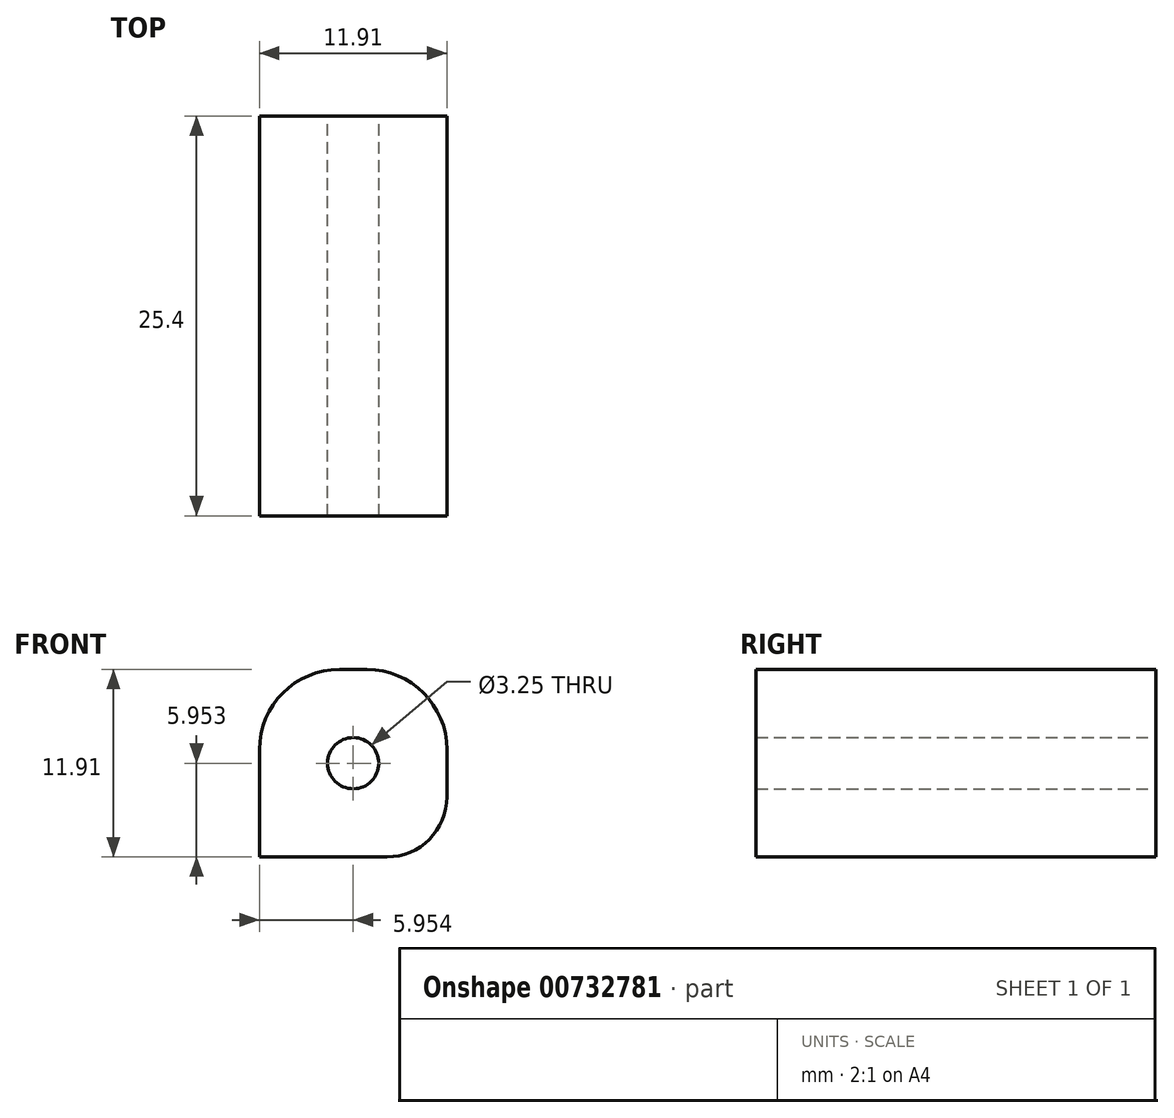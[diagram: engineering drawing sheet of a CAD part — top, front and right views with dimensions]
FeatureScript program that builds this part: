
annotation { "Feature Type Name" : "Feature", "Feature Type Description" : "" }
export const myFeature = defineFeature(function(context is Context, id is Id, definition is map)
    precondition{}
    {
        {
            var Q0;
            Q0=qCreatedBy(makeId("Front.planeOp"),FACE);
            var sketch = newSketch(context, id + "F0", { "sketchPlane" : qUnion([Q0])});
            skPoint(sketch, "E0", {"position": v(-4.1, 3.6) * mm});
            skCircle(sketch, "E1", {"center": v(-4.1, 3.6) * mm, "radius": 1.63 * mm});
            skCircle(sketch, "E2", {"center": v(-4.1, 3.6) * mm, "radius": 5.95 * mm});
            skLineSegment(sketch, "E3", {"start": v(-10.06, 3.6) * mm, "end": v(-10.06, -2.36) * mm});
            skLineSegment(sketch, "E4", {"start": v(-4.1, -2.36) * mm, "end": v(-10.06, -2.36) * mm});
            skLineSegment(sketch, "E5.MirrorCS", {"start": v(1.85, 3.6) * mm, "end": v(1.85, -2.36) * mm});
            skLineSegment(sketch, "E6.MirrorCS", {"start": v(-4.1, -2.36) * mm, "end": v(1.85, -2.36) * mm});
            skLineSegment(sketch, "E7", {"start": v(1.85, 3.6) * mm, "end": v(1.85, 9.55) * mm});
            skLineSegment(sketch, "E8", {"start": v(1.85, 9.55) * mm, "end": v(-10.06, 9.55) * mm});
            skLineSegment(sketch, "E9", {"start": v(-10.06, 9.55) * mm, "end": v(-10.06, -2.36) * mm});
            skLineSegment(sketch, "E10", {"start": v(-10.06, -2.36) * mm, "end": v(1.85, -2.36) * mm});
            skSolve(sketch);
        }
        {
            var Q0;
            {var subQ0=sQuery(id+"F0.wireOp",EDGE,"E8");var subQ1=sQuery(id+"F0.wireOp",EDGE,"E2");var subQ2=makeQuery(id+"F0.imprint","INTERSECT",VERTEX,{"derivedFrom":[subQ1,subQ0]});Q0=makeQuery(id+"F0.imprint","IMPRINT",FACE,{"disambiguationData":[TD([[makeQuery(id+"F0.imprint","IMPRINT",EDGE,{"disambiguationData":[TD([[subQ2,-1.0]])],"derivedFrom":subQ1}),-1.0]])]});}
            var Q1;
            Q1=makeQuery(id+"F0.imprint","IMPRINT",FACE,{"disambiguationData":[TD([[makeQuery(id+"F0.imprint","IMPRINT",EDGE,{"derivedFrom":sQuery(id+"F0.wireOp",EDGE,"E1")}),-1.0]])]});
            var Q2;
            {var subQ0=sQuery(id+"F0.wireOp",EDGE,"E7");Q2=makeQuery(id+"F0.imprint","IMPRINT",FACE,{"disambiguationData":[TD([[makeQuery(id+"F0.imprint","IMPRINT",EDGE,{"derivedFrom":subQ0}),1.0]])]});}
            var Q3;
            {var subQ0=sQuery(id+"F0.wireOp",EDGE,"E5.MirrorCS");Q3=makeQuery(id+"F0.imprint","IMPRINT",FACE,{"disambiguationData":[TD([[makeQuery(id+"F0.imprint","IMPRINT",EDGE,{"derivedFrom":subQ0}),-1.0]])]});}
            var Q4;
            {var subQ0=sQuery(id+"F0.wireOp",EDGE,"E9");var subQ1=sQuery(id+"F0.wireOp",EDGE,"E2");var subQ2=makeQuery(id+"F0.imprint","INTERSECT",VERTEX,{"derivedFrom":[subQ1,subQ0]});Q4=makeQuery(id+"F0.imprint","IMPRINT",FACE,{"disambiguationData":[TD([[makeQuery(id+"F0.imprint","IMPRINT",EDGE,{"disambiguationData":[TD([[subQ2,-1.0]])],"derivedFrom":subQ1}),-1.0]])]});}
            extrude(context, id + "F1", {"entities" : qUnion([Q0, Q1, Q2, Q3, Q4]), "depth" : 25.4 * mm, "offsetDistance" : 25.4 * mm});
        }
        {
            var Q0;
            Q0=makeQuery(id+"F1.opExtrude","SWEPT_EDGE",EDGE,{"disambiguationData":[OSD([sQuery(id+"F0.wireOp",EDGE,"E7"),sQuery(id+"F0.wireOp",EDGE,"E8")])]});
            var Q1;
            Q1=makeQuery(id+"F1.opExtrude","SWEPT_EDGE",EDGE,{"disambiguationData":[OSD([sQuery(id+"F0.wireOp",EDGE,"E8"),sQuery(id+"F0.wireOp",EDGE,"E9")])]});
            fillet(context, id + "F2", {"entities" : qUnion([Q0, Q1]), "radius" : 5.08 * mm, "tangentPropagation" : true, "allowEdgeOverflow" : false});
        }
        {
            var Q0;
            Q0=makeQuery(id+"F1.opExtrude","SWEPT_EDGE",EDGE,{"disambiguationData":[OSD([sQuery(id+"F0.wireOp",EDGE,"E9"),sQuery(id+"F0.wireOp",EDGE,"E10")])]});
            var Q1;
            Q1=makeQuery(id+"F1.opExtrude","SWEPT_EDGE",EDGE,{"disambiguationData":[OSD([sQuery(id+"F0.wireOp",EDGE,"E5.MirrorCS"),sQuery(id+"F0.wireOp",EDGE,"E10")])]});
            fillet(context, id + "F3", {"entities" : qUnion([Q0, Q1]), "radius" : 3.8 * mm, "tangentPropagation" : true, "allowEdgeOverflow" : false});
        }
    });
